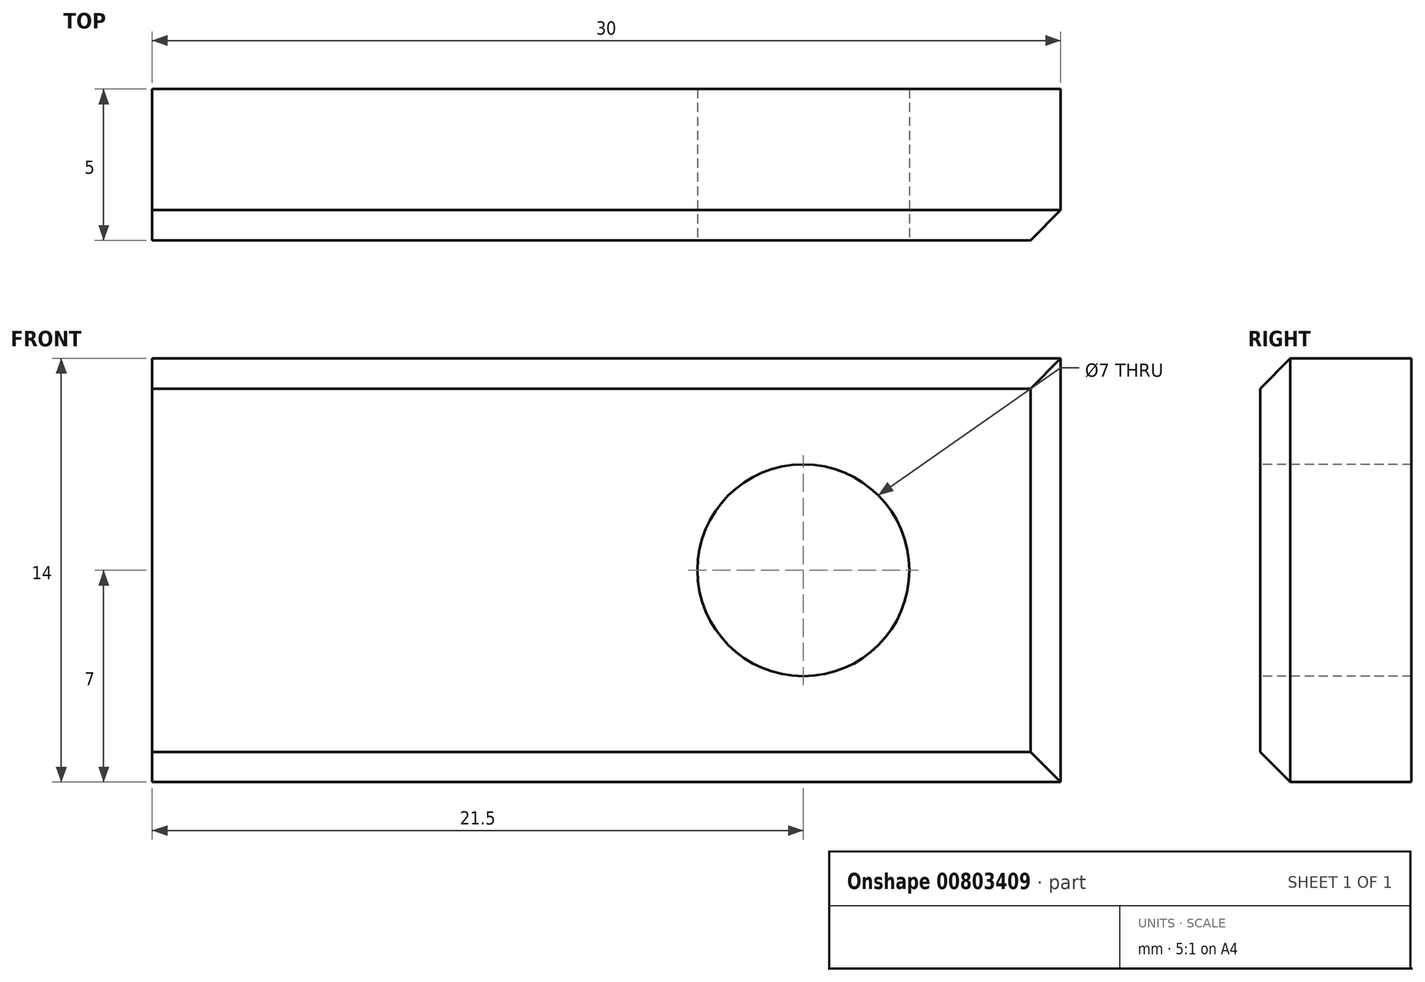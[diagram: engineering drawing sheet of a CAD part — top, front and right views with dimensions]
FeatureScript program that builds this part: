
annotation { "Feature Type Name" : "Feature", "Feature Type Description" : "" }
export const myFeature = defineFeature(function(context is Context, id is Id, definition is map)
    precondition{}
    {
        {
            var Q0;
            Q0=qCreatedBy(makeId("Front.planeOp"),FACE);
            var sketch = newSketch(context, id + "F0", { "sketchPlane" : qUnion([Q0])});
            skLineSegment(sketch, "E0.bottom", {"start": v(0, 0) * mm, "end": v(30, 0) * mm});
            skLineSegment(sketch, "E0.top", {"start": v(0, 14) * mm, "end": v(30, 14) * mm});
            skLineSegment(sketch, "E0.left", {"start": v(0, 0) * mm, "end": v(0, 14) * mm});
            skLineSegment(sketch, "E0.right", {"start": v(30, 0) * mm, "end": v(30, 14) * mm});
            skSolve(sketch);
        }
        {
            var Q0;
            Q0 = qSketchRegion(id + "F0", true);
            extrude(context, id + "F1", {"entities" : qUnion([Q0]), "depth" : 5 * mm, "offsetDistance" : 25 * mm});
        }
        {
            var Q0;
            Q0=makeQuery(id+"F1.opExtrude","CAP_FACE",FACE,{"disambiguationData":[OSD([sQuery(id+"F0.wireOp",EDGE,"E0.bottom"),sQuery(id+"F0.wireOp",EDGE,"E0.top"),sQuery(id+"F0.wireOp",EDGE,"E0.left"),sQuery(id+"F0.wireOp",EDGE,"E0.right")])],"isStart":false});
            var sketch = newSketch(context, id + "F2", { "sketchPlane" : qUnion([Q0])});
            skLineSegment(sketch, "E1", {"start": v(30, 0) * mm, "end": v(30, 7) * mm});
            skLineSegment(sketch, "E2", {"start": v(30, 7) * mm, "end": v(21.5, 7) * mm});
            skCircle(sketch, "E3", {"center": v(21.5, 7) * mm, "radius": 3.5 * mm});
            skSolve(sketch);
        }
        {
            var Q0;
            Q0=makeQuery(id+"F2.imprint","IMPRINT",FACE,{"disambiguationData":[TD([[makeQuery(id+"F2.imprint","IMPRINT",EDGE,{"derivedFrom":sQuery(id+"F2.wireOp",EDGE,"E3")}),1.0]])]});
            extrude(context, id + "F3", {"entities" : qUnion([Q0]), "operationType" : NewBodyOperationType.REMOVE, "endBound" : BoundingType.THROUGH_ALL, "oppositeDirection" : true, "depth" : 25 * mm, "offsetDistance" : 25 * mm});
        }
        {
            var Q0;
            Q0=makeQuery(id+"F1.opExtrude","CAP_EDGE",EDGE,{"disambiguationData":[OSD([sQuery(id+"F0.wireOp",EDGE,"E0.top")])],"isStart":false});
            var Q1;
            Q1=makeQuery(id+"F1.opExtrude","CAP_EDGE",EDGE,{"disambiguationData":[OSD([sQuery(id+"F0.wireOp",EDGE,"E0.right")])],"isStart":false});
            var Q2;
            Q2=makeQuery(id+"F1.opExtrude","CAP_EDGE",EDGE,{"disambiguationData":[OSD([sQuery(id+"F0.wireOp",EDGE,"E0.bottom")])],"isStart":false});
            chamfer(context, id + "F4", {"entities" : qUnion([Q0, Q1, Q2]), "width" : 1 * mm, "tangentPropagation" : true});
        }
    });
